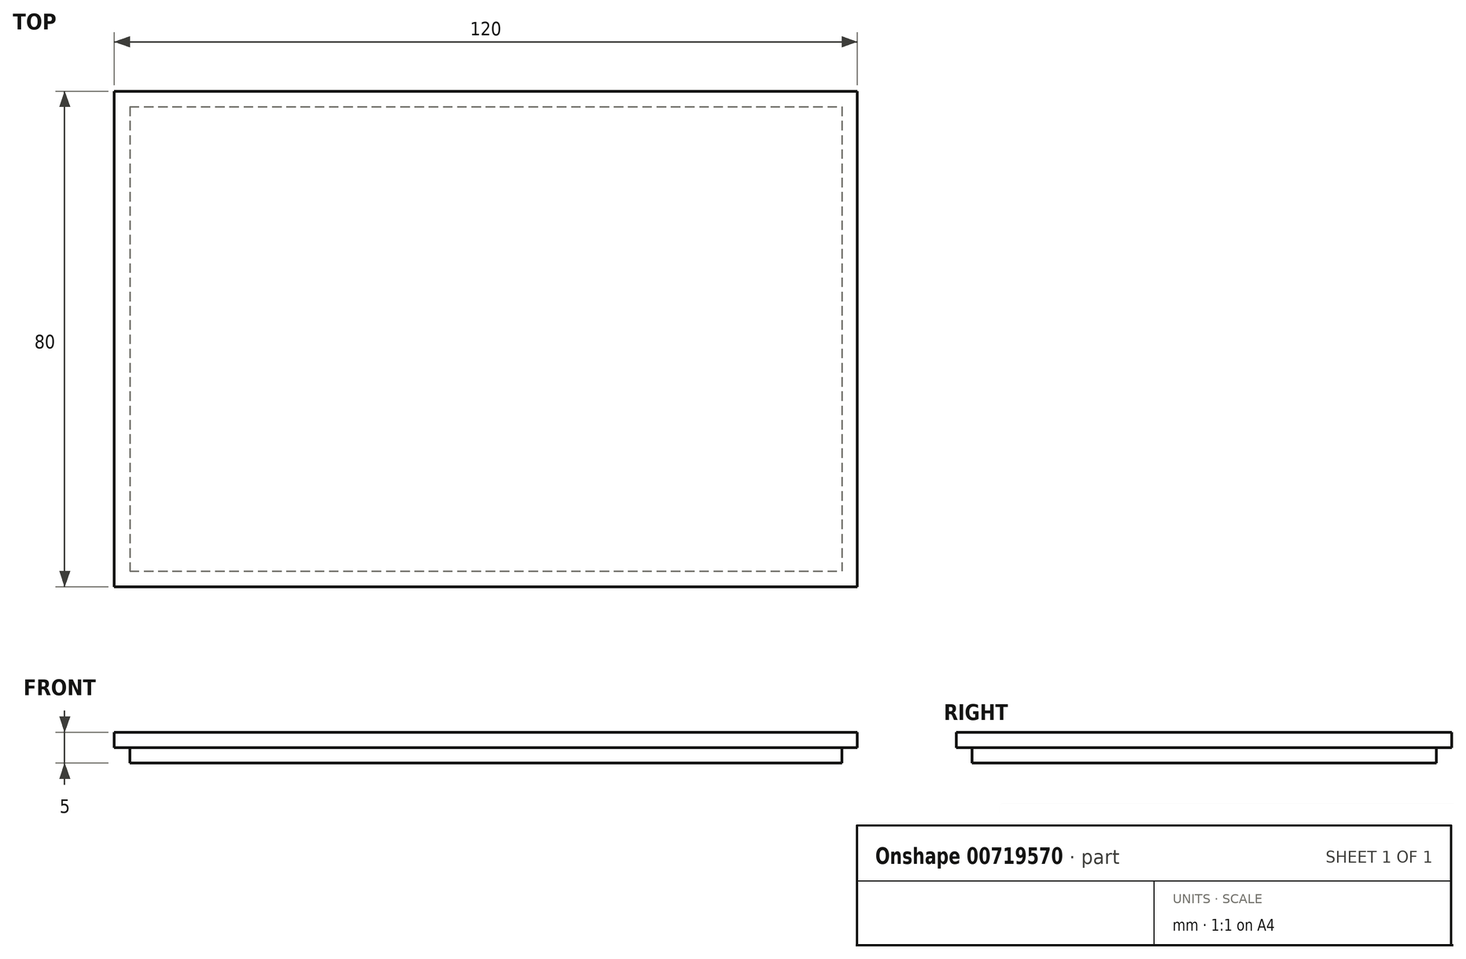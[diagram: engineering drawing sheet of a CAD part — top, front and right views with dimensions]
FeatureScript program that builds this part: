
annotation { "Feature Type Name" : "Feature", "Feature Type Description" : "" }
export const myFeature = defineFeature(function(context is Context, id is Id, definition is map)
    precondition{}
    {
        {
            var Q0;
            Q0=qCreatedBy(makeId("Top.planeOp"),FACE);
            var sketch = newSketch(context, id + "F0", { "sketchPlane" : qUnion([Q0])});
            skLineSegment(sketch, "E0.bottom", {"start": v(-85.54, 47.86) * mm, "end": v(34.46, 47.86) * mm});
            skLineSegment(sketch, "E0.top", {"start": v(-85.54, -32.14) * mm, "end": v(34.46, -32.14) * mm});
            skLineSegment(sketch, "E0.left", {"start": v(-85.54, 47.86) * mm, "end": v(-85.54, -32.14) * mm});
            skLineSegment(sketch, "E0.right", {"start": v(34.46, 47.86) * mm, "end": v(34.46, -32.14) * mm});
            skLineSegment(sketch, "E1.bottom", {"start": v(-83.04, 45.36) * mm, "end": v(31.96, 45.36) * mm});
            skLineSegment(sketch, "E1.top", {"start": v(-83.04, -29.64) * mm, "end": v(31.96, -29.64) * mm});
            skLineSegment(sketch, "E1.left", {"start": v(-83.04, 45.36) * mm, "end": v(-83.04, -29.64) * mm});
            skLineSegment(sketch, "E1.right", {"start": v(31.96, 45.36) * mm, "end": v(31.96, -29.64) * mm});
            skSolve(sketch);
        }
        {
            var Q0;
            Q0=makeQuery(id+"F0.imprint","IMPRINT",FACE,{"disambiguationData":[TD([[makeQuery(id+"F0.imprint","IMPRINT",EDGE,{"derivedFrom":sQuery(id+"F0.wireOp",EDGE,"E0.bottom")}),-1.0]])]});
            extrude(context, id + "F1", {"entities" : qUnion([Q0]), "oppositeDirection" : true, "depth" : 2.5 * mm, "offsetDistance" : 25 * mm});
        }
        {
            var Q0;
            Q0=makeQuery(id+"F0.imprint","IMPRINT",FACE,{"disambiguationData":[TD([[makeQuery(id+"F0.imprint","IMPRINT",EDGE,{"derivedFrom":sQuery(id+"F0.wireOp",EDGE,"E1.bottom")}),-1.0]])]});
            extrude(context, id + "F2", {"entities" : qUnion([Q0]), "operationType" : NewBodyOperationType.ADD, "oppositeDirection" : true, "depth" : 5 * mm, "offsetDistance" : 25 * mm});
        }
    });
